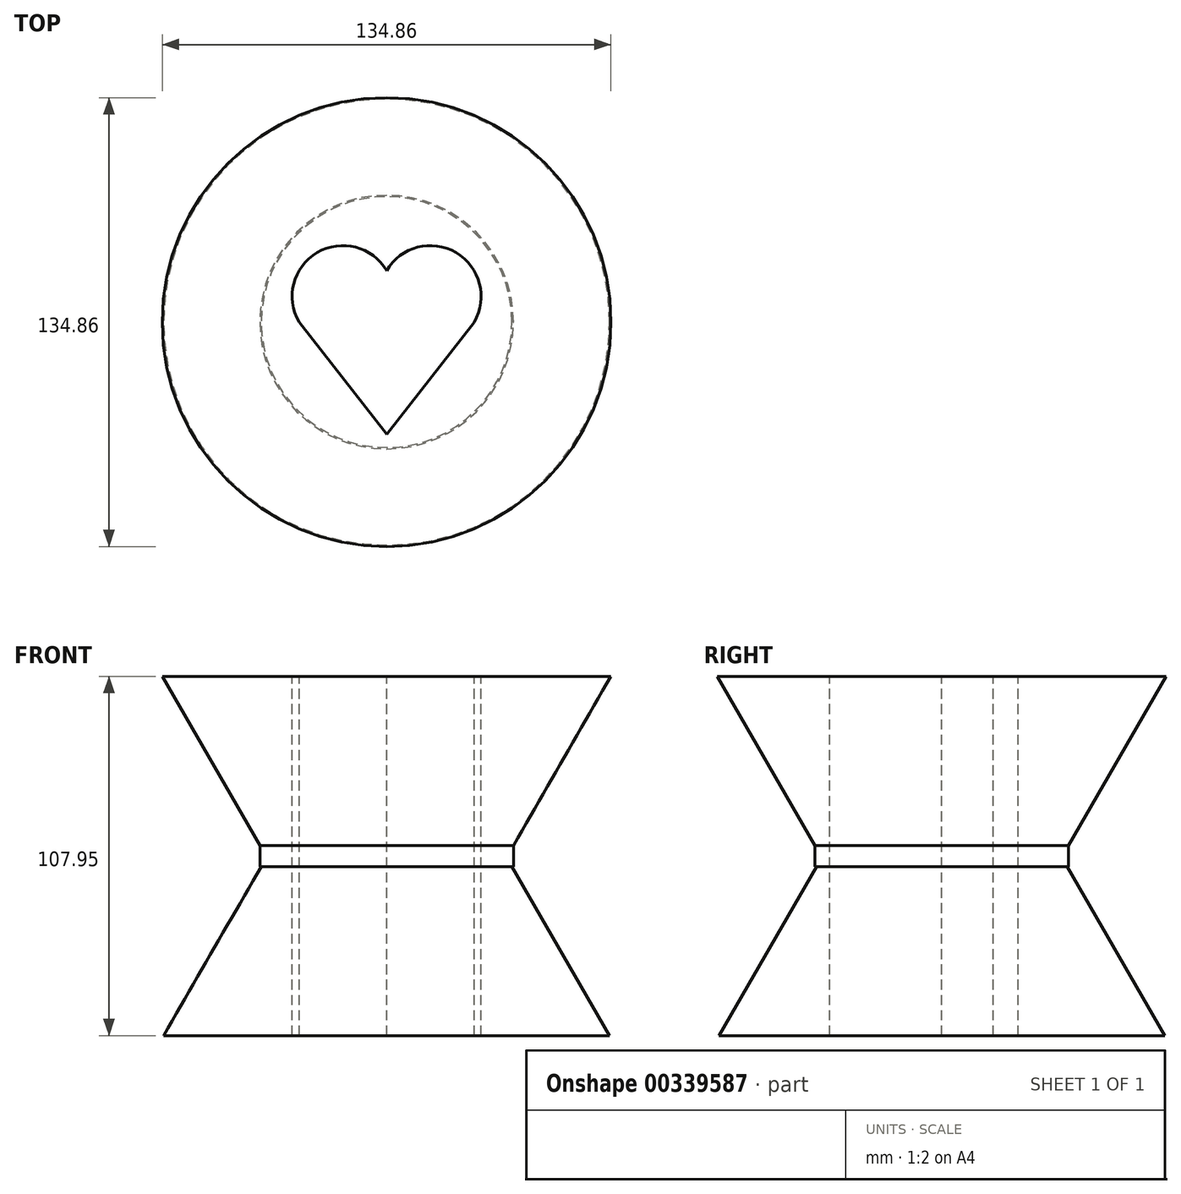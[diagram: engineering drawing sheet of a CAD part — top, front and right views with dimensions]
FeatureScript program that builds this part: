
annotation { "Feature Type Name" : "Feature", "Feature Type Description" : "" }
export const myFeature = defineFeature(function(context is Context, id is Id, definition is map)
    precondition{}
    {
        {
            var Q0;
            Q0=qCreatedBy(makeId("Top.planeOp"),FACE);
            var sketch = newSketch(context, id + "F0", { "sketchPlane" : qUnion([Q0])});
            skCircle(sketch, "E0", {"center": v(0, 0) * mm, "radius": 38.1 * mm});
            skSolve(sketch);
        }
        {
            var Q0;
            Q0 = qSketchRegion(id + "F0", true);
            extrude(context, id + "F1", {"entities" : qUnion([Q0]), "depth" : 50.8 * mm, "hasDraft" : true, "draftAngle" : 30 * degree});
        }
        {
            var Q0;
            Q0 = qSketchRegion(id + "F0", true);
            extrude(context, id + "F2", {"entities" : qUnion([Q0]), "operationType" : NewBodyOperationType.ADD, "oppositeDirection" : true, "depth" : 6.35 * mm});
        }
        {
            var Q0;
            Q0=makeQuery(id+"F2.opExtrude","CAP_FACE",FACE,{"disambiguationData":[OSD([sQuery(id+"F0.wireOp",EDGE,"E0")])],"isStart":false});
            var sketch = newSketch(context, id + "F3", { "sketchPlane" : qUnion([Q0])});
            skCircle(sketch, "E1", {"center": v(0, 0) * mm, "radius": 37.68 * mm});
            skSolve(sketch);
        }
        {
            var Q0;
            Q0 = qSketchRegion(id + "F3", true);
            extrude(context, id + "F4", {"entities" : qUnion([Q0]), "operationType" : NewBodyOperationType.ADD, "depth" : 50.8 * mm, "hasDraft" : true, "draftAngle" : 30 * degree});
        }
        {
            var Q0;
            Q0=makeQuery(id+"F1.opExtrude","CAP_FACE",FACE,{"disambiguationData":[OSD([sQuery(id+"F0.wireOp",EDGE,"E0")])],"isStart":false});
            var sketch = newSketch(context, id + "F5", { "sketchPlane" : qUnion([Q0])});
            skLineSegment(sketch, "E2", {"start": v(0, -33.75) * mm, "end": v(-26.3, 0) * mm});
            skLineSegment(sketch, "E3", {"start": v(0, -33.75) * mm, "end": v(26.3, 0) * mm});
            skArc(sketch, "E4", {"start": v(0, 15.47) * mm, "mid": v(-20.88, 20.88) * mm, "end": v(-26.3, 0) * mm});
            skArc(sketch, "E5", {"start": v(26.3, 0) * mm, "mid": v(20.88, 20.88) * mm, "end": v(0, 15.47) * mm});
            skPoint(sketch, "E6.orphan", {"position": v(0, 0) * mm});
            skSolve(sketch);
        }
        {
            var Q0;
            Q0 = qSketchRegion(id + "F5", true);
            extrude(context, id + "F6", {"entities" : qUnion([Q0]), "operationType" : NewBodyOperationType.REMOVE, "oppositeDirection" : true, "depth" : 127 * mm});
        }
    });
